# Revit family: TEMID_Шлагбаум_BGM1045R
name_source: partatom
category: Охранная сигнализация
units: mm (PartAtom-declared; Revit-internal decimal feet)

## family parameters
Всегда вертикально = Нет
На основе рабочей плоскости = Нет
Общий = Да
При загрузке вырезать с полостями = Нет
Размер круглого соединителя = Использовать диаметр
Сохранять ориентацию аннотаций = Нет
Тип детали = Нормальный
Точка расчета площади = Да

## types (1)
- BGM1045R_Стрела_Правая_Подъём стандарт
    =Габариты= = =Габариты=
    =Стрела= = =Стрела=
    ADSK_Единица измерения = шт.
    ADSK_Завод-изготовитель = TEMID
    ADSK_Классификация нагрузок = Прочее
    ADSK_Количество = 1
    ADSK_Количество фаз = 1
    ADSK_Коэффициент мощности = 0.95
    ADSK_Марка = BGM1045R
    ADSK_Наименование = Шлагбаум электромеханический со стрелой 4.5м телескоп., бесщеточный двигатель,время подъема 5 c, 220В (120 Вт), с блоком управления, индикацией шлагбаума,  -35 ~ +70 град.С., правый, Bluetooth, APP ZKBarrier.
    ADSK_Напряжение = 220 В
    ADSK_Номинальная мощность = 120 Вт
    ADSK_Обозначение = RD
    ADSK_Полная мощность = 126 В·А
    ADSK_Раздел спецификации = 3. Периферийное оборудование
    ADSK_Размер_Высота = 1010 мм
    ADSK_Размер_Глубина = 280 мм
    ADSK_Размер_Ширина = 350 мм
    ADSK_Тип = BGM1045R
    ADSK_Ток = 574.163 мА
    URL = https://temid-global.ru
    Зона обслуживания_Отступ от прибора = 250 мм
    Материал боковины стрелы = Красный
    Материал буквы_Стрела закрыта = Зеленый
    Материал буквы_Стрела открыта = Красный
    Материал стойки = Черный
    Материал стрелы = Белый
    Отметка по умолчанию = 0 мм
    Стрела основание_Высота = 150 мм
    Стрела основание_Глубина = 50 мм
    Стрела основание_Ширина = 150 мм
    Стрела подъём Г образный = Нет
    Стрела подъём стандартный = Да
    Стрела_Высота снования = 700 мм
    Стрела_Глубина = 40 мм
    Стрела_Длина 1 участка = 45 мм
    Стрела_Длина 2 участка = 4095 мм
    Стрела_Длина общая = 4500 мм
    Стрела_Левая = Нет
    Стрела_Правая = Да
    Стрела_Ширина = 50 мм
    УГО_Тип = УГО_СС_Универсальный_текст_прямоугольный : УГО_СС_Шлагбаум
    Угол 1_закрытой стрелы = 90.00°
    Угол 1_открытой стрелы = 180.00°
    Угол 2_закрытой стрелы = 90.00°
    Угол 2_открытой стрелы = 90.00°
